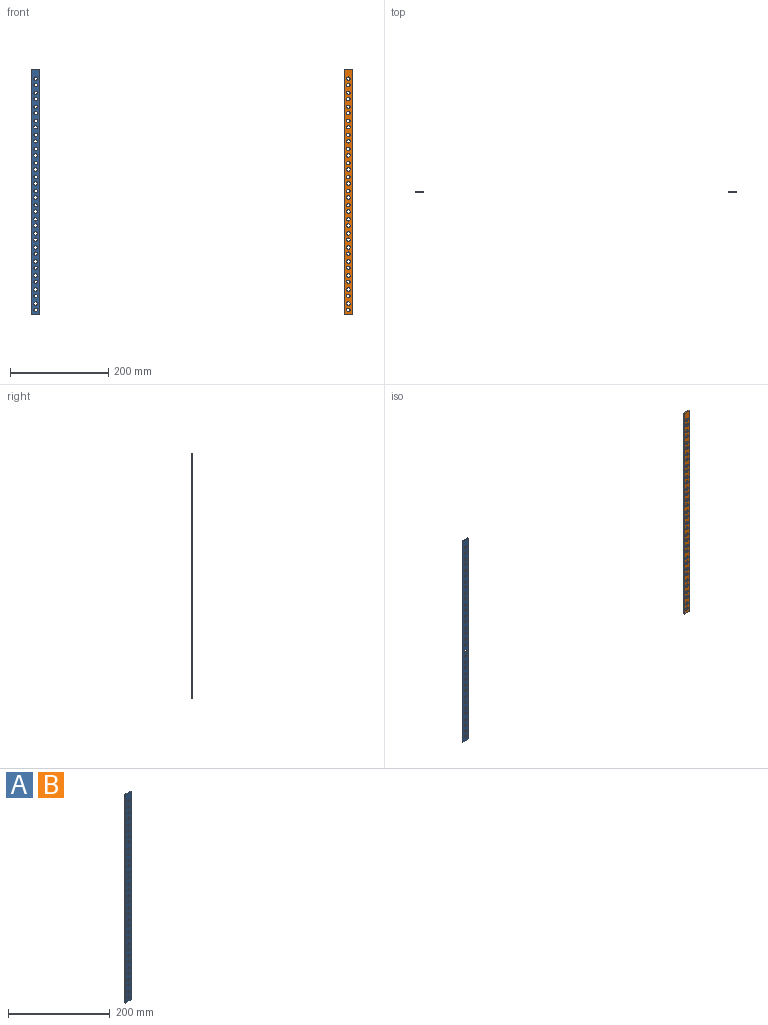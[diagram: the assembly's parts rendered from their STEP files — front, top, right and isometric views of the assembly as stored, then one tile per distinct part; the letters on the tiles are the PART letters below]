
ASSEMBLY  parts=2 mates=1
PART A: 40 faces, bbox 16.5x2x500 mm
  f0: plane 16.5x2mm, normal (0,0,-1), area 33mm2, adj f1,f3,f4,f5
  f1: plane 500x2mm, normal (1,0,0), area 1000mm2, adj f0,f2,f4,f5
  f2: plane 16.5x2mm, normal (0,0,1), area 33mm2, adj f1,f3,f4,f5
  f3: plane 500x2mm, normal (-1,0,0), area 1000mm2, adj f0,f2,f4,f5
  f4: plane 500x16.5mm, normal (0,1,0), area 6903.9mm2, adj f0,f1,f2,f3,f6,f7,f8,f9
  f5: plane 500x16.5mm, normal (0,-1,0), area 6903.9mm2, adj f0,f1,f2,f3,f6,f7,f8,f9
  f6: cylinder r=3.55mm len=7.1mm, axis (0,-1,0), area 44.6mm2, adj f4,f5
  f7: cylinder r=3.55mm len=7.1mm, axis (0,-1,0), area 44.6mm2, adj f4,f5
  f8: cylinder r=3.55mm len=7.1mm, axis (0,-1,0), area 44.6mm2, adj f4,f5
  f9: cylinder r=3.55mm len=7.1mm, axis (0,-1,0), area 44.6mm2, adj f4,f5
  f10: cylinder r=3.55mm len=7.1mm, axis (0,-1,0), area 44.6mm2, adj f4,f5
  f11: cylinder r=3.55mm len=7.1mm, axis (0,-1,0), area 44.6mm2, adj f4,f5
  f12: cylinder r=3.55mm len=7.1mm, axis (0,-1,0), area 44.6mm2, adj f4,f5
  f13: cylinder r=3.55mm len=7.1mm, axis (0,-1,0), area 44.6mm2, adj f4,f5
  f14: cylinder r=3.55mm len=7.1mm, axis (0,-1,0), area 44.6mm2, adj f4,f5
  f15: cylinder r=3.55mm len=7.1mm, axis (0,-1,0), area 44.6mm2, adj f4,f5
  f16: cylinder r=3.55mm len=7.1mm, axis (0,-1,0), area 44.6mm2, adj f4,f5
  f17: cylinder r=3.55mm len=7.1mm, axis (0,-1,0), area 44.6mm2, adj f4,f5
  f18: cylinder r=3.55mm len=7.1mm, axis (0,-1,0), area 44.6mm2, adj f4,f5
  f19: cylinder r=3.55mm len=7.1mm, axis (0,-1,0), area 44.6mm2, adj f4,f5
  f20: cylinder r=3.55mm len=7.1mm, axis (0,-1,0), area 44.6mm2, adj f4,f5
  f21: cylinder r=3.55mm len=7.1mm, axis (0,-1,0), area 44.6mm2, adj f4,f5
  f22: cylinder r=3.55mm len=7.1mm, axis (0,-1,0), area 44.6mm2, adj f4,f5
  f23: cylinder r=3.55mm len=7.1mm, axis (0,-1,0), area 44.6mm2, adj f4,f5
  f24: cylinder r=3.55mm len=7.1mm, axis (0,-1,0), area 44.6mm2, adj f4,f5
  f25: cylinder r=3.55mm len=7.1mm, axis (0,-1,0), area 44.6mm2, adj f4,f5
  f26: cylinder r=3.55mm len=7.1mm, axis (0,-1,0), area 44.6mm2, adj f4,f5
  f27: cylinder r=3.55mm len=7.1mm, axis (0,-1,0), area 44.6mm2, adj f4,f5
  f28: cylinder r=3.55mm len=7.1mm, axis (0,-1,0), area 44.6mm2, adj f4,f5
  f29: cylinder r=3.55mm len=7.1mm, axis (0,-1,0), area 44.6mm2, adj f4,f5
  f30: cylinder r=3.55mm len=7.1mm, axis (0,-1,0), area 44.6mm2, adj f4,f5
  f31: cylinder r=3.55mm len=7.1mm, axis (0,-1,0), area 44.6mm2, adj f4,f5
  f32: cylinder r=3.55mm len=7.1mm, axis (0,-1,0), area 44.6mm2, adj f4,f5
  f33: cylinder r=3.55mm len=7.1mm, axis (0,-1,0), area 44.6mm2, adj f4,f5
  f34: cylinder r=3.55mm len=7.1mm, axis (0,-1,0), area 44.6mm2, adj f4,f5
  f35: cylinder r=3.55mm len=7.1mm, axis (0,-1,0), area 44.6mm2, adj f4,f5
  f36: cylinder r=3.55mm len=7.1mm, axis (0,-1,0), area 44.6mm2, adj f4,f5
  f37: cylinder r=3.55mm len=7.1mm, axis (0,-1,0), area 44.6mm2, adj f4,f5
  f38: cylinder r=3.55mm len=7.1mm, axis (0,-1,0), area 44.6mm2, adj f4,f5
  f39: cylinder r=3.55mm len=7.1mm, axis (0,-1,0), area 44.6mm2, adj f4,f5
PART B: same geometry as A
PLACE A at identity
PLACE B t=(636.5,0,0)mm
MATE fastened A.f0 <-> B.f0  axis (0,0,1) through (0,0,0)mm
